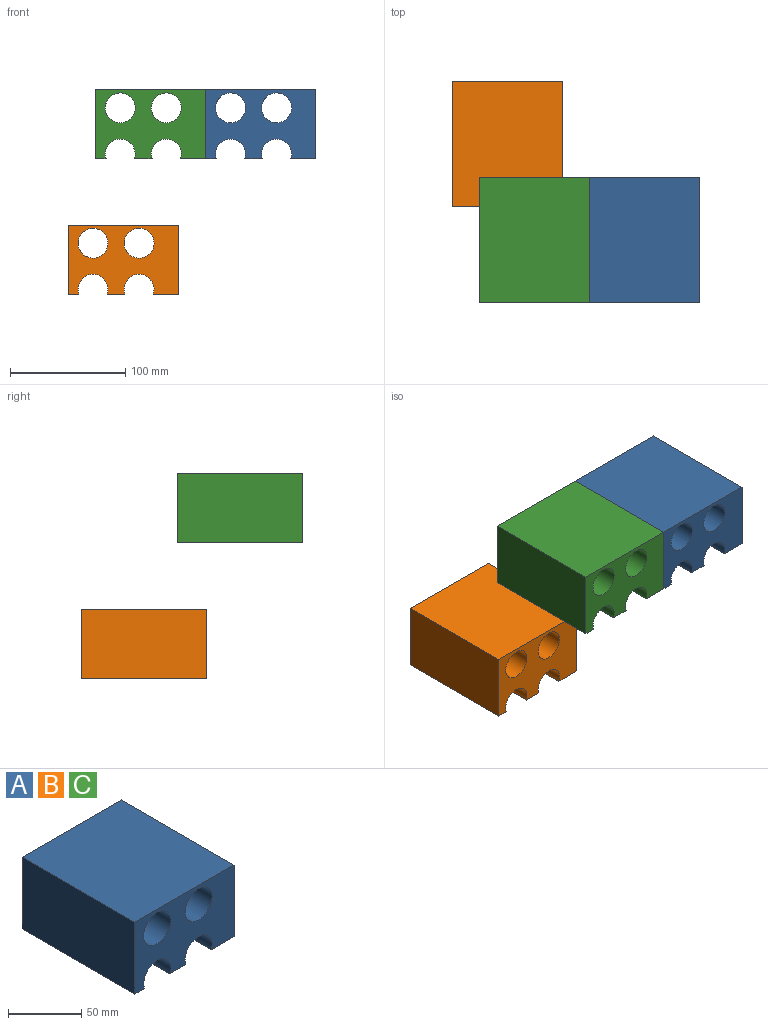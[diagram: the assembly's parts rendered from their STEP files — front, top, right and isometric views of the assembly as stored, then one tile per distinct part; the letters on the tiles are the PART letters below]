
ASSEMBLY  parts=3 mates=1
PART A: 12 faces, bbox 95.8x108.9x60 mm
  f0: plane 95.81x60mm, normal (0,-1,0), area 3938mm2, adj f1,f2,f3,f4,f6,f7,f8,f9
  f1: plane 108.94x9.39mm, normal (0,0,-1), area 1023.2mm2, adj f0,f3,f5,f9
  f2: plane 108.94x15.47mm, normal (0,0,-1), area 1685.5mm2, adj f0,f5,f8,f9
  f3: plane 108.94x60mm, normal (-1,0,0), area 6536.3mm2, adj f0,f1,f5,f6
  f4: plane 108.94x60mm, normal (1,0,0), area 6536.3mm2, adj f0,f5,f6,f7
  f5: plane 95.81x60mm, normal (0,1,0), area 3938mm2, adj f1,f2,f3,f4,f6,f7,f8,f9
  f6: plane 108.94x95.81mm, normal (0,0,1), area 10437.6mm2, adj f0,f3,f4,f5
  f7: plane 108.94x21.89mm, normal (0,0,-1), area 2384.9mm2, adj f0,f4,f5,f8
  f8: cylinder r=12.99mm len=108.94mm, axis (0,-1,0), area 5401.5mm2, adj f0,f2,f5,f7
  f9: cylinder r=12.99mm len=108.94mm, axis (0,-1,0), area 5401.5mm2, adj f0,f1,f2,f5
  f10: cylinder r=12.99mm len=108.94mm, axis (0,-1,0), area 8894.7mm2, adj f0,f5
  f11: cylinder r=12.99mm len=108.94mm, axis (0,-1,0), area 8894.7mm2, adj f0,f5
PART B: same geometry as A
PART C: same geometry as A
PLACE A t=(105.56,-67.03,116.65)mm
PLACE B t=(-13.89,16.51,-0.86)mm
PLACE C t=(9.74,-67.03,116.65)mm
MATE fastened C.f4 <-> A.f3  axis (1,0,0) through (62.13,-69.55,146.65)mm
